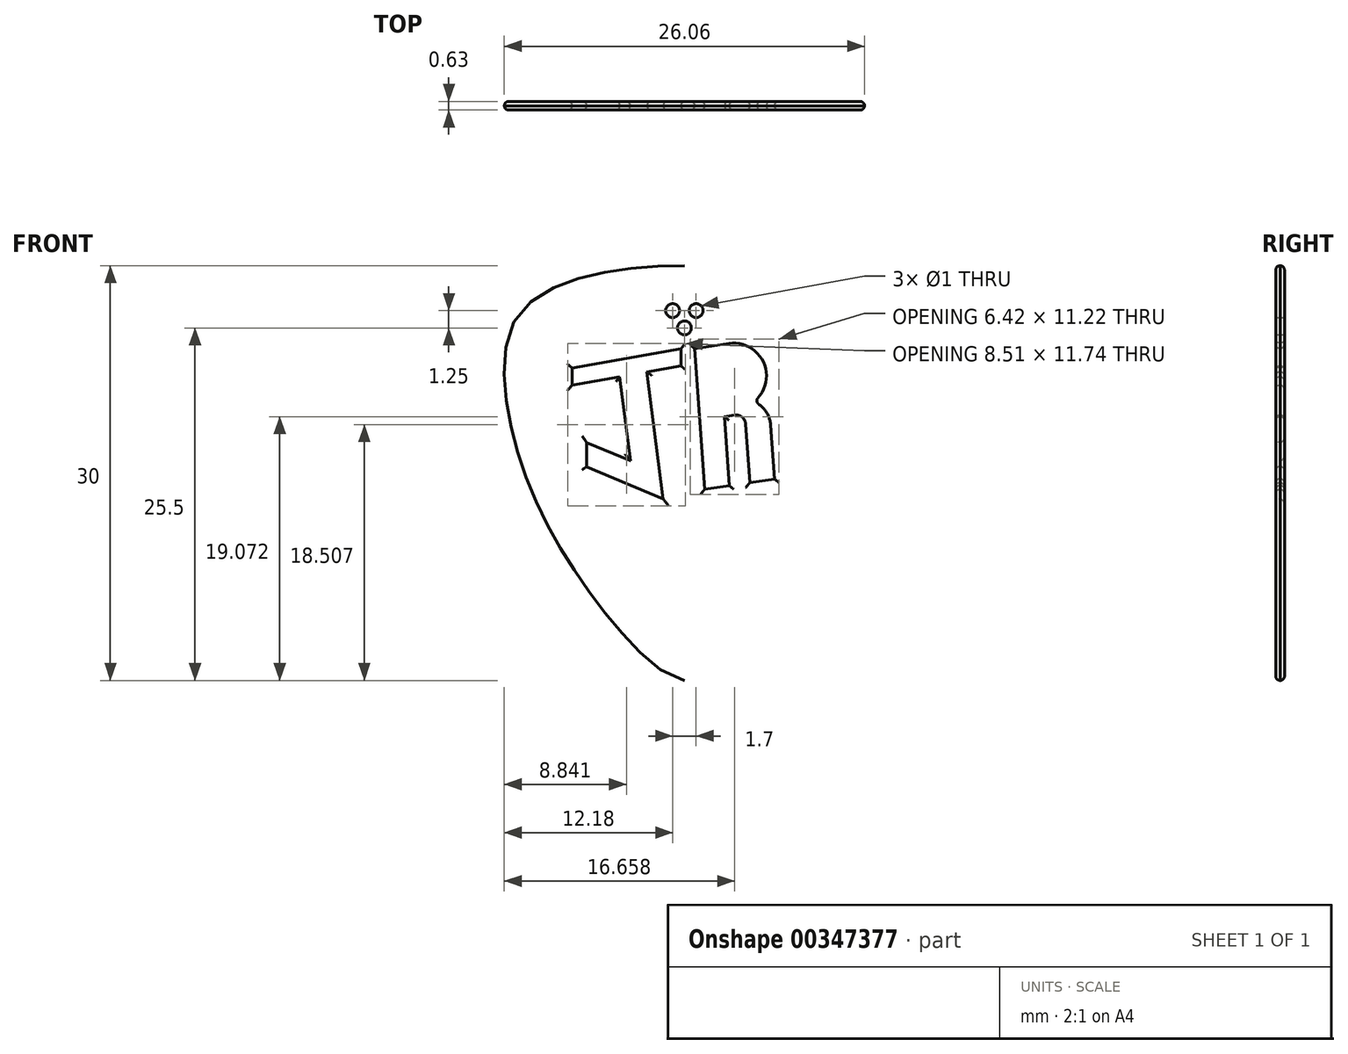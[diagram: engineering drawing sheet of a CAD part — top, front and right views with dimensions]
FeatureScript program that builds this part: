
annotation { "Feature Type Name" : "Feature", "Feature Type Description" : "" }
export const myFeature = defineFeature(function(context is Context, id is Id, definition is map)
    precondition{}
    {
        {
            var Q0;
            Q0=qCreatedBy(makeId("Front.planeOp"),FACE);
            var sketch = newSketch(context, id + "F0", { "sketchPlane" : qUnion([Q0])});
            skLineSegment(sketch, "E0", {"start": v(0, 0) * mm, "end": v(0, 6.75) * mm, "construction": true});
            skLineSegment(sketch, "E1", {"start": v(0, 0) * mm, "end": v(0, -23.25) * mm, "construction": true});
            skLineSegment(sketch, "E2", {"start": v(0, 0) * mm, "end": v(13, 0) * mm, "construction": true});
            skFitSpline(sketch, "E3", {"points": [v(0, -23.25) * mm, v(9.5, -12.75) * mm, v(13, 0) * mm, v(11, 4.25) * mm, v(0, 6.75) * mm], "startDerivative": vector(20.6, 0) * mm, "endDerivative": vector(-57.72, 0) * mm});
            skFitSpline(sketch, "E4.MirrorCS", {"points": [v(0, -23.25) * mm, v(-9.5, -12.75) * mm, v(-13, 0) * mm, v(-11, 4.25) * mm, v(0, 6.75) * mm], "startDerivative": vector(-20.6, 0) * mm, "endDerivative": vector(57.72, 0) * mm});
            skLineSegment(sketch, "E5", {"start": v(0, 3.5) * mm, "end": v(0.85, 3.5) * mm});
            skCircle(sketch, "E6", {"center": v(0.85, 3.5) * mm, "radius": 0.5 * mm});
            skLineSegment(sketch, "E7.MirrorCS", {"start": v(0, 3.5) * mm, "end": v(-0.85, 3.5) * mm});
            skCircle(sketch, "E8.MirrorC", {"center": v(-0.85, 3.5) * mm, "radius": 0.5 * mm});
            skLineSegment(sketch, "E9", {"start": v(0.75, 0.75) * mm, "end": v(1.46, -9.43) * mm});
            skLineSegment(sketch, "E10", {"start": v(1.46, -9.43) * mm, "end": v(3.24, -9.16) * mm});
            skLineSegment(sketch, "E11", {"start": v(3.24, -9.16) * mm, "end": v(2.9, -4.17) * mm});
            skLineSegment(sketch, "E12", {"start": v(2.9, -4.17) * mm, "end": v(3.63, -4.06) * mm});
            skLineSegment(sketch, "E13", {"start": v(4.73, -8.94) * mm, "end": v(4.43, -4.7) * mm});
            skLineSegment(sketch, "E14", {"start": v(3.24, -9.16) * mm, "end": v(4.73, -8.94) * mm, "construction": true});
            skLineSegment(sketch, "E15", {"start": v(4.73, -8.94) * mm, "end": v(6.5, -8.67) * mm});
            skArc(sketch, "E16", {"start": v(4.43, -4.7) * mm, "mid": v(4.17, -4.2) * mm, "end": v(3.63, -4.06) * mm});
            skLineSegment(sketch, "E17", {"start": v(6.5, -8.67) * mm, "end": v(6.23, -4.78) * mm});
            skLineSegment(sketch, "E18", {"start": v(0.75, 0.75) * mm, "end": v(3.22, 1.12) * mm});
            skArc(sketch, "E19", {"start": v(5.03, -3.08) * mm, "mid": v(5.74, -0.29) * mm, "end": v(3.22, 1.12) * mm});
            skArc(sketch, "E20", {"start": v(6.23, -4.78) * mm, "mid": v(5.87, -3.76) * mm, "end": v(5.03, -3.08) * mm});
            skLineSegment(sketch, "E21", {"start": v(-2.7, -0.93) * mm, "end": v(-1.54, -10.1) * mm});
            skLineSegment(sketch, "E22", {"start": v(-1.54, -10.1) * mm, "end": v(-7.08, -7.79) * mm});
            skLineSegment(sketch, "E23", {"start": v(-7.08, -7.79) * mm, "end": v(-7.08, -6.04) * mm});
            skLineSegment(sketch, "E24", {"start": v(-7.08, -6.04) * mm, "end": v(-3.9, -7.37) * mm});
            skLineSegment(sketch, "E25", {"start": v(-3.9, -7.37) * mm, "end": v(-4.68, -1.28) * mm});
            skLineSegment(sketch, "E26", {"start": v(-4.68, -1.28) * mm, "end": v(-8.13, -1.89) * mm});
            skLineSegment(sketch, "E27", {"start": v(-8.13, -1.89) * mm, "end": v(-8.13, -0.64) * mm});
            skLineSegment(sketch, "E28", {"start": v(-8.13, -0.64) * mm, "end": v(-0.25, 0.75) * mm});
            skLineSegment(sketch, "E29", {"start": v(-0.25, 0.75) * mm, "end": v(-0.25, -0.5) * mm});
            skLineSegment(sketch, "E30", {"start": v(-0.25, -0.5) * mm, "end": v(-2.7, -0.93) * mm});
            skLineSegment(sketch, "E31", {"start": v(-4.68, -1.28) * mm, "end": v(-2.7, -0.93) * mm, "construction": true});
            skCircle(sketch, "E32", {"center": v(0, 2.25) * mm, "radius": 0.5 * mm});
            skSolve(sketch);
        }
        {
            var Q0;
            Q0=qSketchRegion(id+"F0",true);
            extrude(context, id + "F1", {"entities" : qUnion([Q0]), "depth" : 0.63 * mm});
        }
        {
            var Q0;
            Q0=makeQuery(id+"F1.opExtrude","CAP_EDGE",EDGE,{"disambiguationData":[OSD([sQuery(id+"F0.wireOp",EDGE,"E4.MirrorCS")])],"isStart":false});
            var Q1;
            Q1=makeQuery(id+"F1.opExtrude","CAP_EDGE",EDGE,{"disambiguationData":[OSD([sQuery(id+"F0.wireOp",EDGE,"E3")])],"isStart":false});
            var Q2;
            Q2=makeQuery(id+"F1.opExtrude","CAP_EDGE",EDGE,{"disambiguationData":[OSD([sQuery(id+"F0.wireOp",EDGE,"E4.MirrorCS")])],"isStart":true});
            var Q3;
            Q3=makeQuery(id+"F1.opExtrude","CAP_EDGE",EDGE,{"disambiguationData":[OSD([sQuery(id+"F0.wireOp",EDGE,"E3")])],"isStart":true});
            fillet(context, id + "F2", {"entities" : qUnion([Q0, Q1, Q2, Q3]), "radius" : 0.63 / 2 * mm, "tangentPropagation" : true, "allowEdgeOverflow" : false});
        }
        {
            var Q0;
            Q0=makeQuery(id+"F1.opExtrude","CAP_EDGE",EDGE,{"disambiguationData":[OSD([sQuery(id+"F0.wireOp",EDGE,"E24")])],"isStart":false});
            var Q1;
            Q1=makeQuery(id+"F1.opExtrude","CAP_EDGE",EDGE,{"disambiguationData":[OSD([sQuery(id+"F0.wireOp",EDGE,"E25")])],"isStart":false});
            var Q2;
            Q2=makeQuery(id+"F1.opExtrude","CAP_EDGE",EDGE,{"disambiguationData":[OSD([sQuery(id+"F0.wireOp",EDGE,"E23")])],"isStart":false});
            var Q3;
            Q3=makeQuery(id+"F1.opExtrude","CAP_EDGE",EDGE,{"disambiguationData":[OSD([sQuery(id+"F0.wireOp",EDGE,"E22")])],"isStart":false});
            var Q4;
            Q4=makeQuery(id+"F1.opExtrude","CAP_EDGE",EDGE,{"disambiguationData":[OSD([sQuery(id+"F0.wireOp",EDGE,"E21")])],"isStart":false});
            var Q5;
            Q5=makeQuery(id+"F1.opExtrude","CAP_EDGE",EDGE,{"disambiguationData":[OSD([sQuery(id+"F0.wireOp",EDGE,"E30")])],"isStart":false});
            var Q6;
            Q6=makeQuery(id+"F1.opExtrude","CAP_EDGE",EDGE,{"disambiguationData":[OSD([sQuery(id+"F0.wireOp",EDGE,"E29")])],"isStart":false});
            var Q7;
            Q7=makeQuery(id+"F1.opExtrude","CAP_EDGE",EDGE,{"disambiguationData":[OSD([sQuery(id+"F0.wireOp",EDGE,"E28")])],"isStart":false});
            var Q8;
            Q8=makeQuery(id+"F1.opExtrude","CAP_EDGE",EDGE,{"disambiguationData":[OSD([sQuery(id+"F0.wireOp",EDGE,"E27")])],"isStart":false});
            var Q9;
            Q9=makeQuery(id+"F1.opExtrude","CAP_EDGE",EDGE,{"disambiguationData":[OSD([sQuery(id+"F0.wireOp",EDGE,"E26")])],"isStart":false});
            var Q10;
            Q10=makeQuery(id+"F1.opExtrude","CAP_EDGE",EDGE,{"disambiguationData":[OSD([sQuery(id+"F0.wireOp",EDGE,"E18")])],"isStart":false});
            var Q11;
            Q11=makeQuery(id+"F1.opExtrude","CAP_EDGE",EDGE,{"disambiguationData":[OSD([sQuery(id+"F0.wireOp",EDGE,"E19")])],"isStart":false});
            var Q12;
            Q12=makeQuery(id+"F1.opExtrude","CAP_EDGE",EDGE,{"disambiguationData":[OSD([sQuery(id+"F0.wireOp",EDGE,"E9")])],"isStart":false});
            var Q13;
            Q13=makeQuery(id+"F1.opExtrude","CAP_EDGE",EDGE,{"disambiguationData":[OSD([sQuery(id+"F0.wireOp",EDGE,"E10")])],"isStart":false});
            var Q14;
            Q14=makeQuery(id+"F1.opExtrude","CAP_EDGE",EDGE,{"disambiguationData":[OSD([sQuery(id+"F0.wireOp",EDGE,"E11")])],"isStart":false});
            var Q15;
            Q15=makeQuery(id+"F1.opExtrude","CAP_EDGE",EDGE,{"disambiguationData":[OSD([sQuery(id+"F0.wireOp",EDGE,"E12")])],"isStart":false});
            var Q16;
            Q16=makeQuery(id+"F1.opExtrude","CAP_EDGE",EDGE,{"disambiguationData":[OSD([sQuery(id+"F0.wireOp",EDGE,"E15")])],"isStart":false});
            var Q17;
            Q17=makeQuery(id+"F1.opExtrude","CAP_EDGE",EDGE,{"disambiguationData":[OSD([sQuery(id+"F0.wireOp",EDGE,"E17")])],"isStart":false});
            var Q18;
            Q18=makeQuery(id+"F1.opExtrude","CAP_EDGE",EDGE,{"disambiguationData":[OSD([sQuery(id+"F0.wireOp",EDGE,"E20")])],"isStart":false});
            var Q19;
            Q19=makeQuery(id+"F1.opExtrude","CAP_EDGE",EDGE,{"disambiguationData":[OSD([sQuery(id+"F0.wireOp",EDGE,"E15")])],"isStart":true});
            var Q20;
            Q20=makeQuery(id+"F1.opExtrude","CAP_EDGE",EDGE,{"disambiguationData":[OSD([sQuery(id+"F0.wireOp",EDGE,"E13")])],"isStart":true});
            var Q21;
            Q21=makeQuery(id+"F1.opExtrude","CAP_EDGE",EDGE,{"disambiguationData":[OSD([sQuery(id+"F0.wireOp",EDGE,"E17")])],"isStart":true});
            var Q22;
            Q22=makeQuery(id+"F1.opExtrude","CAP_EDGE",EDGE,{"disambiguationData":[OSD([sQuery(id+"F0.wireOp",EDGE,"E19")])],"isStart":true});
            var Q23;
            Q23=makeQuery(id+"F1.opExtrude","CAP_EDGE",EDGE,{"disambiguationData":[OSD([sQuery(id+"F0.wireOp",EDGE,"E18")])],"isStart":true});
            var Q24;
            Q24=makeQuery(id+"F1.opExtrude","CAP_EDGE",EDGE,{"disambiguationData":[OSD([sQuery(id+"F0.wireOp",EDGE,"E9")])],"isStart":true});
            var Q25;
            Q25=makeQuery(id+"F1.opExtrude","CAP_EDGE",EDGE,{"disambiguationData":[OSD([sQuery(id+"F0.wireOp",EDGE,"E12")])],"isStart":true});
            var Q26;
            Q26=makeQuery(id+"F1.opExtrude","CAP_EDGE",EDGE,{"disambiguationData":[OSD([sQuery(id+"F0.wireOp",EDGE,"E11")])],"isStart":true});
            var Q27;
            Q27=makeQuery(id+"F1.opExtrude","CAP_EDGE",EDGE,{"disambiguationData":[OSD([sQuery(id+"F0.wireOp",EDGE,"E10")])],"isStart":true});
            var Q28;
            Q28=makeQuery(id+"F1.opExtrude","CAP_EDGE",EDGE,{"disambiguationData":[OSD([sQuery(id+"F0.wireOp",EDGE,"E21")])],"isStart":true});
            var Q29;
            Q29=makeQuery(id+"F1.opExtrude","CAP_EDGE",EDGE,{"disambiguationData":[OSD([sQuery(id+"F0.wireOp",EDGE,"E22")])],"isStart":true});
            var Q30;
            Q30=makeQuery(id+"F1.opExtrude","CAP_EDGE",EDGE,{"disambiguationData":[OSD([sQuery(id+"F0.wireOp",EDGE,"E23")])],"isStart":true});
            var Q31;
            Q31=makeQuery(id+"F1.opExtrude","CAP_EDGE",EDGE,{"disambiguationData":[OSD([sQuery(id+"F0.wireOp",EDGE,"E24")])],"isStart":true});
            var Q32;
            Q32=makeQuery(id+"F1.opExtrude","CAP_EDGE",EDGE,{"disambiguationData":[OSD([sQuery(id+"F0.wireOp",EDGE,"E25")])],"isStart":true});
            var Q33;
            Q33=makeQuery(id+"F1.opExtrude","CAP_EDGE",EDGE,{"disambiguationData":[OSD([sQuery(id+"F0.wireOp",EDGE,"E26")])],"isStart":true});
            var Q34;
            Q34=makeQuery(id+"F1.opExtrude","CAP_EDGE",EDGE,{"disambiguationData":[OSD([sQuery(id+"F0.wireOp",EDGE,"E27")])],"isStart":true});
            var Q35;
            Q35=makeQuery(id+"F1.opExtrude","CAP_EDGE",EDGE,{"disambiguationData":[OSD([sQuery(id+"F0.wireOp",EDGE,"E28")])],"isStart":true});
            var Q36;
            Q36=makeQuery(id+"F1.opExtrude","CAP_EDGE",EDGE,{"disambiguationData":[OSD([sQuery(id+"F0.wireOp",EDGE,"E30")])],"isStart":true});
            var Q37;
            Q37=makeQuery(id+"F1.opExtrude","CAP_EDGE",EDGE,{"disambiguationData":[OSD([sQuery(id+"F0.wireOp",EDGE,"E29")])],"isStart":true});
            var Q38;
            Q38=makeQuery(id+"F1.opExtrude","SWEPT_EDGE",EDGE,{"disambiguationData":[OSD([sQuery(id+"F0.wireOp",EDGE,"E19"),sQuery(id+"F0.wireOp",EDGE,"E20")])]});
            fillet(context, id + "F3", {"entities" : qUnion([Q0, Q1, Q2, Q3, Q4, Q5, Q6, Q7, Q8, Q9, Q10, Q11, Q12, Q13, Q14, Q15, Q16, Q17, Q18, Q19, Q20, Q21, Q22, Q23, Q24, Q25, Q26, Q27, Q28, Q29, Q30, Q31, Q32, Q33, Q34, Q35, Q36, Q37, Q38]), "radius" : (0.63 / 2) * mm, "tangentPropagation" : true, "allowEdgeOverflow" : false});
        }
    });
